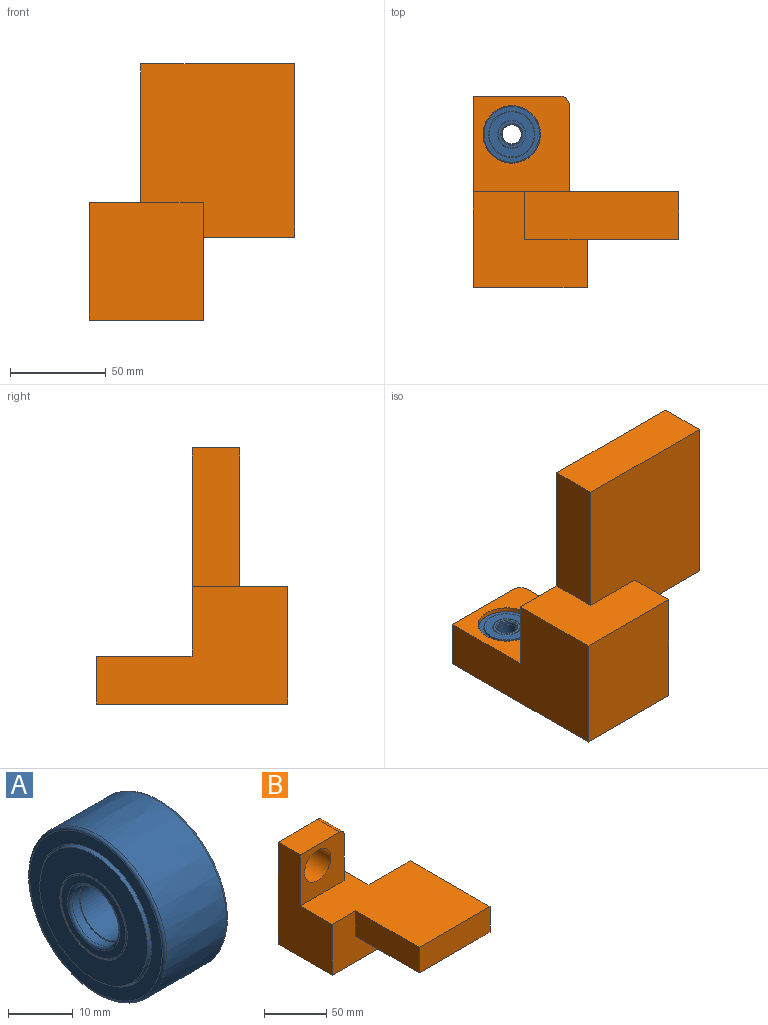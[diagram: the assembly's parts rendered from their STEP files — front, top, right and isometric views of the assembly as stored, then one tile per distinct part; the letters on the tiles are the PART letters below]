
ASSEMBLY  parts=2 mates=1
PART A: 30 faces, bbox 15x32.4x32.4 mm
  f0: torus R=7.05mm, axis (1,0,0), area 17.8mm2, adj f1,f29
  f1: plane 14.1x14.1mm, normal (-1,0,0), area 54.1mm2, adj f0,f2
  f2: torus R=5.7mm, axis (1,0,0), area 26.6mm2, adj f1,f3
  f3: cylinder r=5.2mm len=10.4mm, axis (1,0,0), area 50.8mm2, adj f2,f4
  f4: plane 10.4x10.4mm, normal (-1,0,0), area 6.4mm2, adj f3,f5
  f5: cylinder r=5mm len=10.89mm, axis (1,0,0), area 342.1mm2, adj f4,f6
  f6: plane 10.4x10.4mm, normal (1,0,0), area 6.4mm2, adj f5,f7
  f7: cylinder r=5.2mm len=10.4mm, axis (1,0,0), area 50.8mm2, adj f6,f8
  f8: torus R=5.7mm, axis (1,0,0), area 26.6mm2, adj f7,f9
  f9: plane 14.1x14.1mm, normal (1,0,0), area 54.1mm2, adj f8,f10
  f10: torus R=7.05mm, axis (1,0,0), area 17.8mm2, adj f9,f11
  f11: cylinder r=7.3mm len=14.6mm, axis (1,0,0), area 11.5mm2, adj f10,f12
  f12: plane 14.7x14.7mm, normal (1,0,0), area 2.3mm2, adj f11,f13
  f13: cylinder r=7.35mm len=14.7mm, axis (1,0,0), area 23.1mm2, adj f12,f14
  f14: plane 23.5x23.5mm, normal (1,0,0), area 264mm2, adj f13,f15
  f15: cylinder r=11.75mm len=23.5mm, axis (1,0,0), area 151.8mm2, adj f14,f16
  f16: plane 24.21x24.21mm, normal (1,0,0), area 26.4mm2, adj f15,f17
  f17: cylinder r=12.1mm len=24.21mm, axis (1,0,0), area 118.3mm2, adj f16,f18
  f18: plane 28.92x28.92mm, normal (1,0,0), area 196.5mm2, adj f17,f19
  f19: torus R=14.46mm, axis (1,0,0), area 72.3mm2, adj f18,f20
  f20: revolved ~30x30mm, area 1225.3mm2, adj f19,f21
  f21: torus R=14.46mm, axis (1,0,0), area 72.3mm2, adj f20,f22
  f22: plane 28.92x28.92mm, normal (-1,0,0), area 196.5mm2, adj f21,f23
  f23: cylinder r=12.1mm len=24.21mm, axis (1,0,0), area 118.3mm2, adj f22,f24
  f24: plane 24.21x24.21mm, normal (-1,0,0), area 26.4mm2, adj f23,f25
  f25: cylinder r=11.75mm len=23.5mm, axis (1,0,0), area 151.8mm2, adj f24,f26
  f26: plane 23.5x23.5mm, normal (-1,0,0), area 264mm2, adj f25,f27
  f27: cylinder r=7.35mm len=14.7mm, axis (1,0,0), area 23.1mm2, adj f26,f28
  f28: plane 14.7x14.7mm, normal (-1,0,0), area 2.3mm2, adj f27,f29
  f29: cylinder r=7.3mm len=14.6mm, axis (1,0,0), area 11.5mm2, adj f0,f28
PART B: 16 faces, bbox 106.9x133.4x100 mm
  f0: plane 59.28x50mm, normal (0,-1,0), area 2151mm2, adj f1,f3,f9,f10,f11,f15
  f1: plane 61.26x50mm, normal (1,0,0), area 2613.1mm2, adj f0,f6,f9,f10,f14,f15
  f2: plane 45x25mm, normal (0,0,1), area 1125mm2, adj f3,f5,f6,f7
  f3: plane 100x61.26mm, normal (-1,0,0), area 4312.8mm2, adj f0,f2,f5,f6,f9,f15
  f4: plane 45x25mm, normal (1,0,0), area 1125mm2, adj f5,f6,f7,f9
  f5: plane 50x50mm, normal (0,-1,0), area 1787.8mm2, adj f2,f3,f4,f7,f8,f9
  f6: plane 100x59.28mm, normal (0,1,0), area 4751.6mm2, adj f1,f2,f3,f4,f7,f8,f9,f15
  f7: cylinder r=5mm len=25mm, axis (0,-1,0), area 196.3mm2, adj f2,f4,f5,f6
  f8: cylinder r=15mm len=30mm, axis (0,-1,0), area 2356.2mm2, adj f5,f6
  f9: plane 133.44x106.92mm, normal (0,0,1), area 9024.4mm2, adj f0,f1,f3,f4,f5,f6,f11,f12
  f10: plane 90.17x80.16mm, normal (0,0,-1), area 6643.4mm2, adj f0,f1,f11,f12,f13,f14
  f11: plane 72.18x25mm, normal (-1,0,0), area 1804.6mm2, adj f0,f9,f10,f12
  f12: plane 80.16x25mm, normal (0,-1,0), area 2004.1mm2, adj f9,f10,f11,f13
  f13: plane 90.17x25mm, normal (1,0,0), area 2254.3mm2, adj f9,f10,f12,f14
  f14: plane 47.65x25mm, normal (0,1,0), area 1191.2mm2, adj f1,f9,f10,f13
  f15: plane 61.26x59.28mm, normal (0,0,-1), area 3631mm2, adj f0,f1,f3,f6
PLACE A rot(axis=(0.71,0,0.71),180deg) t=(0,0,-16.51)mm
PLACE B rot(axis=(-1,0,0),90deg) t=(-20,-30,-25)mm
MATE slider A.f0 <-> B.f8  axis (0,0,1) through (0,0,-15.51)mm
